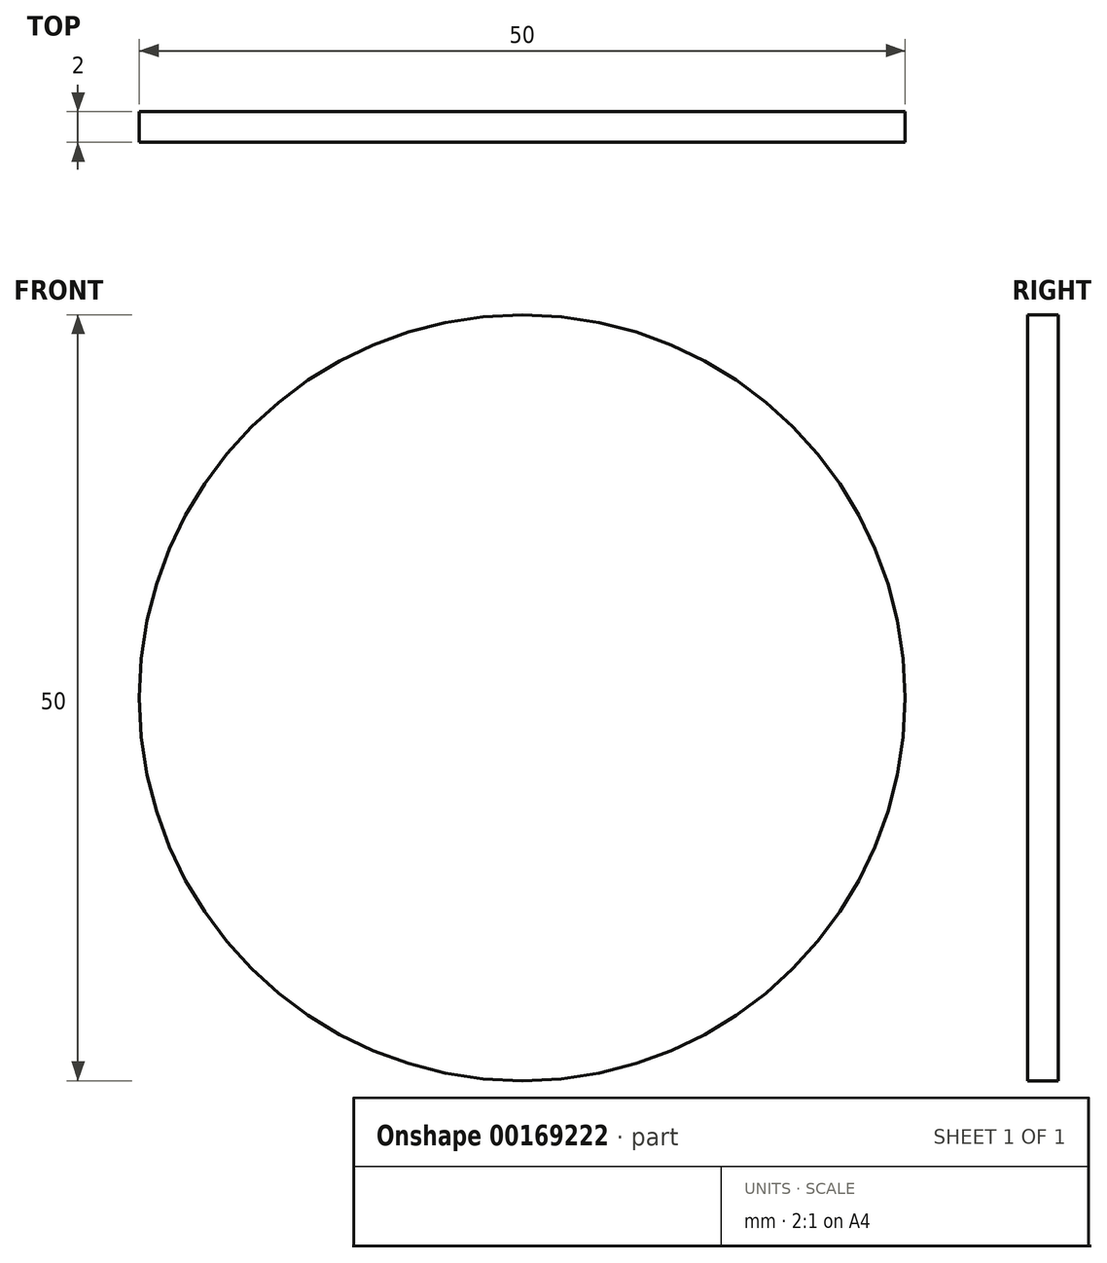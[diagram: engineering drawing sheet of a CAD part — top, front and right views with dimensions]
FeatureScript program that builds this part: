
annotation { "Feature Type Name" : "Feature", "Feature Type Description" : "" }
export const myFeature = defineFeature(function(context is Context, id is Id, definition is map)
    precondition{}
    {
        {
            var Q0;
            Q0=qCreatedBy(makeId("Front.planeOp"),FACE);
            var sketch = newSketch(context, id + "F0", { "sketchPlane" : qUnion([Q0])});
            skCircle(sketch, "E0", {"center": v(0, 0) * mm, "radius": 25 * mm});
            skSolve(sketch);
        }
        {
            var Q0;
            Q0=makeQuery(id+"F0.imprint","IMPRINT",FACE,{"disambiguationData":[TD([[makeQuery(id+"F0.imprint","IMPRINT",EDGE,{"derivedFrom":sQuery(id+"F0.wireOp",EDGE,"E0")}),1.0]])]});
            extrude(context, id + "F1", {"entities" : qUnion([Q0]), "depth" : 2 * mm});
        }
    });
